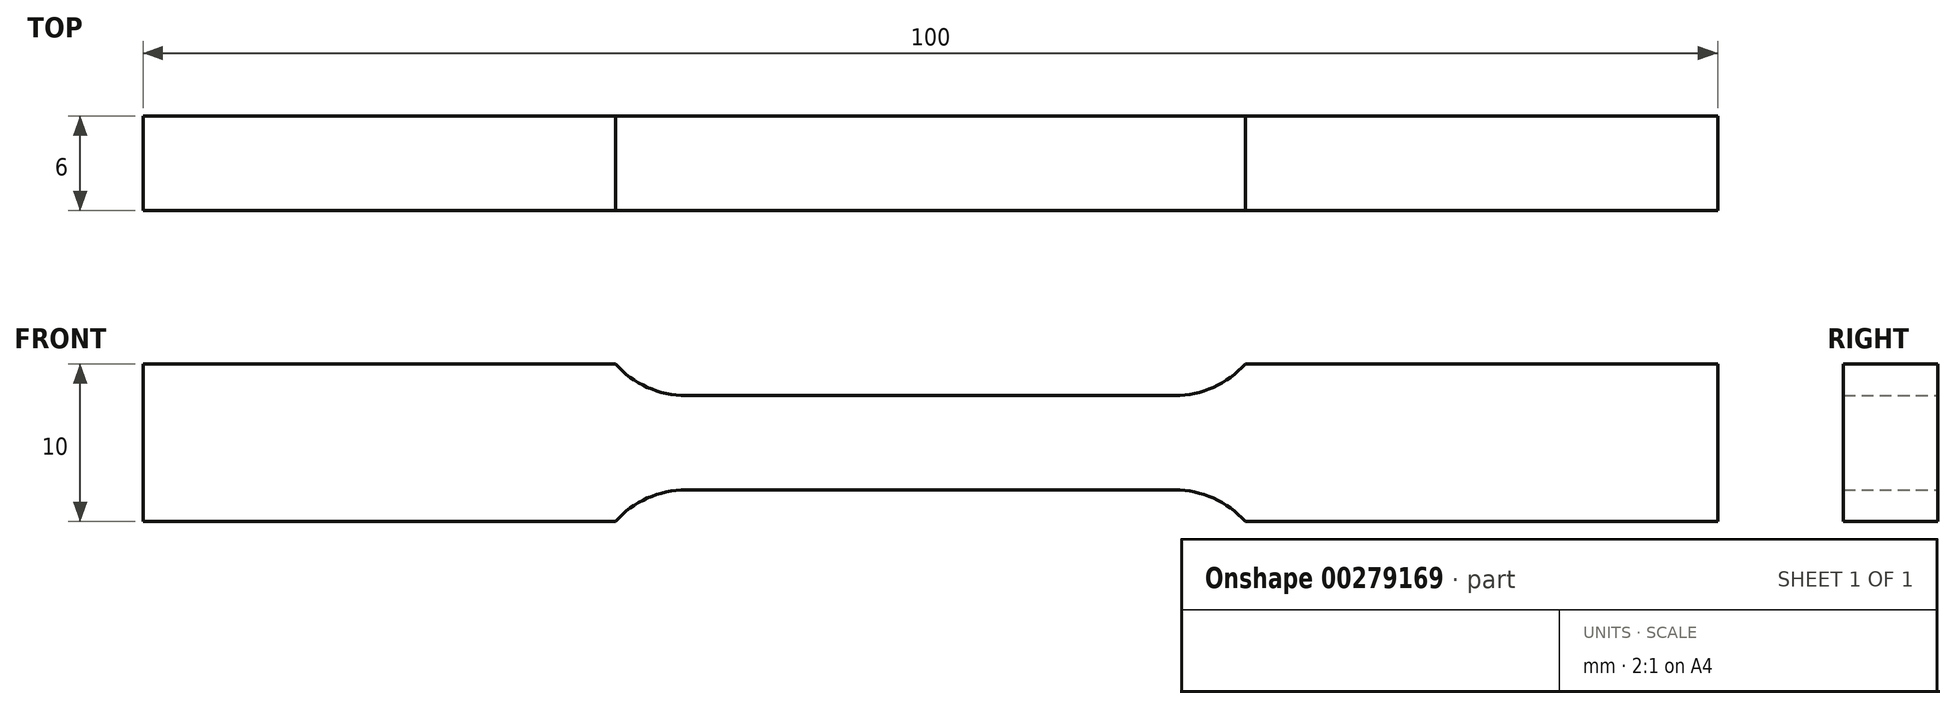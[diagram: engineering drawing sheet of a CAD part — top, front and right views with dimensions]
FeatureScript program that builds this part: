
annotation { "Feature Type Name" : "Feature", "Feature Type Description" : "" }
export const myFeature = defineFeature(function(context is Context, id is Id, definition is map)
    precondition{}
    {
        {
            var Q0;
            Q0=qCreatedBy(makeId("Front.planeOp"),FACE);
            var sketch = newSketch(context, id + "F0", { "sketchPlane" : qUnion([Q0])});
            skLineSegment(sketch, "E0", {"start": v(0, 3) * mm, "end": v(15.53, 3) * mm});
            skArc(sketch, "E1", {"start": v(15.53, 3) * mm, "mid": v(17.98, 3.52) * mm, "end": v(20, 5) * mm});
            skLineSegment(sketch, "E2", {"start": v(20, 5) * mm, "end": v(50, 5) * mm});
            skLineSegment(sketch, "E3", {"start": v(50, 5) * mm, "end": v(50, 0) * mm});
            skLineSegment(sketch, "E4.MirrorCS", {"start": v(50, -5) * mm, "end": v(50, 0) * mm});
            skLineSegment(sketch, "E5.MirrorCS", {"start": v(0, -3) * mm, "end": v(15.53, -3) * mm});
            skLineSegment(sketch, "E6.MirrorCS", {"start": v(20, -5) * mm, "end": v(50, -5) * mm});
            skArc(sketch, "E7.MirrorCS", {"start": v(15.53, -3) * mm, "mid": v(17.98, -3.52) * mm, "end": v(20, -5) * mm});
            skArc(sketch, "E8.MirrorCS", {"start": v(-15.53, -3) * mm, "mid": v(-17.98, -3.52) * mm, "end": v(-20, -5) * mm});
            skLineSegment(sketch, "E9.MirrorCS", {"start": v(-20, -5) * mm, "end": v(-50, -5) * mm});
            skLineSegment(sketch, "E10.MirrorCS", {"start": v(0, 3) * mm, "end": v(-15.53, 3) * mm});
            skArc(sketch, "E11.MirrorCS", {"start": v(-15.53, 3) * mm, "mid": v(-17.98, 3.52) * mm, "end": v(-20, 5) * mm});
            skLineSegment(sketch, "E12.MirrorCS", {"start": v(-20, 5) * mm, "end": v(-50, 5) * mm});
            skLineSegment(sketch, "E13.MirrorCS", {"start": v(-50, 5) * mm, "end": v(-50, 0) * mm});
            skLineSegment(sketch, "E14.MirrorCS", {"start": v(0, -3) * mm, "end": v(-15.53, -3) * mm});
            skLineSegment(sketch, "E15.MirrorCS", {"start": v(-50, -5) * mm, "end": v(-50, 0) * mm});
            skSolve(sketch);
        }
        {
            var Q0;
            Q0=makeQuery(id+"F0.imprint","IMPRINT",FACE,{"disambiguationData":[TD([[makeQuery(id+"F0.imprint","IMPRINT",EDGE,{"derivedFrom":sQuery(id+"F0.wireOp",EDGE,"E0")}),-1.0]])]});
            extrude(context, id + "F1", {"entities" : qUnion([Q0]), "endBound" : BoundingType.SYMMETRIC, "depth" : 6 * mm});
        }
    });
